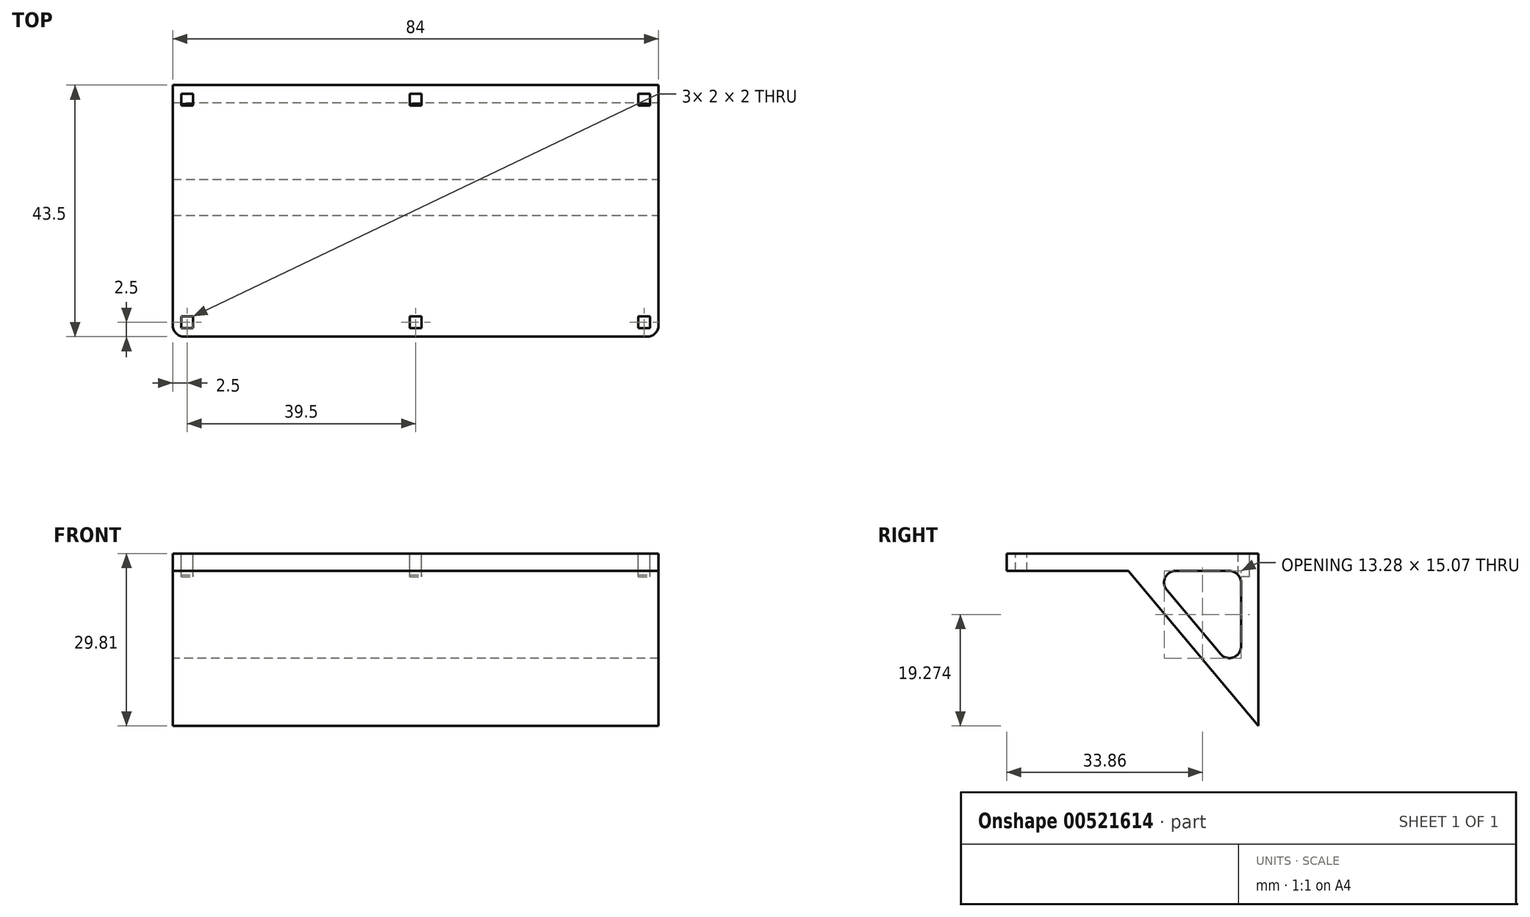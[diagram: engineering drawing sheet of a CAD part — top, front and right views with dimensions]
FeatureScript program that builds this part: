
annotation { "Feature Type Name" : "Feature", "Feature Type Description" : "" }
export const myFeature = defineFeature(function(context is Context, id is Id, definition is map)
    precondition{}
    {
        {
            var Q0;
            Q0=qCreatedBy(makeId("Right.planeOp"),FACE);
            var sketch = newSketch(context, id + "F0", { "sketchPlane" : qUnion([Q0])});
            skLineSegment(sketch, "E0", {"start": v(0, 0) * mm, "end": v(21, 0) * mm});
            skLineSegment(sketch, "E1", {"start": v(21, 0) * mm, "end": v(43.5, -26.81) * mm});
            skLineSegment(sketch, "E2.0", {"start": v(0, 3) * mm, "end": v(21, 3) * mm});
            skLineSegment(sketch, "E3.0", {"start": v(24.92, 0) * mm, "end": v(40.5, -18.57) * mm});
            skLineSegment(sketch, "E4", {"start": v(0, 3) * mm, "end": v(0, 0) * mm});
            skLineSegment(sketch, "E5", {"start": v(21, 3) * mm, "end": v(43.5, 3) * mm});
            skLineSegment(sketch, "E6", {"start": v(43.5, -26.81) * mm, "end": v(43.5, 3) * mm});
            skLineSegment(sketch, "E7", {"start": v(24.92, 0) * mm, "end": v(40.5, 0) * mm});
            skLineSegment(sketch, "E8.trimOffspring", {"start": v(40.5, -18.57) * mm, "end": v(40.5, 0) * mm});
            skSolve(sketch);
        }
        {
            var Q0;
            Q0=makeQuery(id+"F0.imprint","IMPRINT",FACE,{"disambiguationData":[TD([[makeQuery(id+"F0.imprint","IMPRINT",EDGE,{"derivedFrom":sQuery(id+"F0.wireOp",EDGE,"HT0NIHEq-mOGw-AMZ3-bg6D-jiP4Rz8PsHoc.bottom")}),1.0]])]});
            var Q1;
            Q1=makeQuery(id+"F0.imprint","IMPRINT",FACE,{"disambiguationData":[TD([[makeQuery(id+"F0.imprint","IMPRINT",EDGE,{"derivedFrom":sQuery(id+"F0.wireOp",EDGE,"E0")}),1.0]])]});
            var Q2;
            Q2=makeQuery(id+"F0.imprint","IMPRINT",FACE,{"disambiguationData":[TD([[makeQuery(id+"F0.imprint","IMPRINT",EDGE,{"derivedFrom":sQuery(id+"F0.wireOp",EDGE,"E2.0")}),1.0]])]});
            var Q3;
            {var subQ3=sQuery(id+"F0.wireOp",EDGE,"2d6a4896-3aa3-4e97-b98b-c350a894f704.0");Q3=makeQuery(id+"F0.imprint","IMPRINT",FACE,{"disambiguationData":[TD([[makeQuery(id+"F0.imprint","IMPRINT",EDGE,{"derivedFrom":subQ3}),1.0]])]});}
            extrude(context, id + "F1", {"entities" : qUnion([Q0, Q1, Q2, Q3]), "oppositeDirection" : true, "depth" : 84 * mm, "offsetDistance" : 25 * mm});
        }
        {
            var Q0;
            Q0=makeQuery(id+"F1.opExtrude","CAP_EDGE",EDGE,{"disambiguationData":[OSD([sQuery(id+"F0.wireOp",EDGE,"E4"),sQuery(id+"F0.wireOp",EDGE,"HT0NIHEq-mOGw-AMZ3-bg6D-jiP4Rz8PsHoc.left"),sQuery(id+"F0.wireOp",EDGE,"zdLE2qqB-wnvT-7mFk-4lY0-9LTzI25NRc8D")])],"isStart":true});
            var Q1;
            Q1=makeQuery(id+"F1.opExtrude","CAP_EDGE",EDGE,{"disambiguationData":[OSD([sQuery(id+"F0.wireOp",EDGE,"E4"),sQuery(id+"F0.wireOp",EDGE,"HT0NIHEq-mOGw-AMZ3-bg6D-jiP4Rz8PsHoc.left"),sQuery(id+"F0.wireOp",EDGE,"zdLE2qqB-wnvT-7mFk-4lY0-9LTzI25NRc8D")])],"isStart":false});
            var Q2;
            Q2=makeQuery(id+"F1.opExtrude","CAP_EDGE",EDGE,{"disambiguationData":[OSD([sQuery(id+"F0.wireOp",EDGE,"HT0NIHEq-mOGw-AMZ3-bg6D-jiP4Rz8PsHoc.right"),sQuery(id+"F0.wireOp",EDGE,"6K6W7r0D-Gj0a-smYx-N5Y3-3RsnSGkDnLhq")])],"isStart":true});
            var Q3;
            Q3=makeQuery(id+"F1.opExtrude","CAP_EDGE",EDGE,{"disambiguationData":[OSD([sQuery(id+"F0.wireOp",EDGE,"HT0NIHEq-mOGw-AMZ3-bg6D-jiP4Rz8PsHoc.right"),sQuery(id+"F0.wireOp",EDGE,"6K6W7r0D-Gj0a-smYx-N5Y3-3RsnSGkDnLhq")])],"isStart":false});
            fillet(context, id + "F2", {"entities" : qUnion([Q0, Q1, Q2, Q3]), "radius" : 2 * mm, "tangentPropagation" : true, "allowEdgeOverflow" : false});
        }
        {
            var Q0;
            Q0=makeQuery(id+"F1.opExtrude","SWEPT_EDGE",EDGE,{"disambiguationData":[OSD([sQuery(id+"F0.wireOp",EDGE,"E3.0"),sQuery(id+"F0.wireOp",EDGE,"ABOKRz2A-O9Wl-NYz3-LtdV-byAFksUtFqJd")])]});
            var Q1;
            Q1=makeQuery(id+"F1.opExtrude","SWEPT_EDGE",EDGE,{"disambiguationData":[OSD([sQuery(id+"F0.wireOp",EDGE,"E7"),sQuery(id+"F0.wireOp",EDGE,"E8.trimOffspring")])]});
            fillet(context, id + "F3", {"entities" : qUnion([Q0, Q1]), "radius" : 2 * mm, "tangentPropagation" : true, "allowEdgeOverflow" : false});
        }
        {
            var Q0;
            Q0=makeQuery(id+"F1.opExtrude","SWEPT_FACE",FACE,{"disambiguationData":[OSD([sQuery(id+"F0.wireOp",EDGE,"E2.0"),sQuery(id+"F0.wireOp",EDGE,"E5")])]});
            var sketch = newSketch(context, id + "F4", { "sketchPlane" : qUnion([Q0])});
            skLineSegment(sketch, "E9.0.0", {"start": v(-44.5, 43.5) * mm, "end": v(-44.5, 38.5) * mm, "construction": true});
            skLineSegment(sketch, "E9.0.1", {"start": v(-44.5, 38.5) * mm, "end": v(-39.5, 38.5) * mm, "construction": true});
            skLineSegment(sketch, "E9.0.2", {"start": v(-39.5, 38.5) * mm, "end": v(-39.5, 43.5) * mm, "construction": true});
            skLineSegment(sketch, "E9.0.3", {"start": v(-39.5, 43.5) * mm, "end": v(-44.5, 43.5) * mm, "construction": true});
            skLineSegment(sketch, "E10.0.0", {"start": v(0, 38.5) * mm, "end": v(0, 41.5) * mm, "construction": true});
            skArc(sketch, "E10.0.1", {"start": v(0, 41.5) * mm, "mid": v(-0.59, 42.91) * mm, "end": v(-2, 43.5) * mm, "construction": true});
            skLineSegment(sketch, "E10.0.2", {"start": v(-2, 43.5) * mm, "end": v(-5, 43.5) * mm, "construction": true});
            skLineSegment(sketch, "E10.0.3", {"start": v(-5, 43.5) * mm, "end": v(-5, 38.5) * mm, "construction": true});
            skLineSegment(sketch, "E10.0.4", {"start": v(-5, 38.5) * mm, "end": v(0, 38.5) * mm, "construction": true});
            skLineSegment(sketch, "E11.0.0", {"start": v(-5, 0) * mm, "end": v(-2, 0) * mm, "construction": true});
            skArc(sketch, "E11.0.1", {"start": v(-2, 0) * mm, "mid": v(-0.59, 0.59) * mm, "end": v(0, 2) * mm, "construction": true});
            skLineSegment(sketch, "E11.0.2", {"start": v(0, 2) * mm, "end": v(0, 5) * mm, "construction": true});
            skLineSegment(sketch, "E11.0.3", {"start": v(0, 5) * mm, "end": v(-5, 5) * mm, "construction": true});
            skLineSegment(sketch, "E11.0.4", {"start": v(-5, 5) * mm, "end": v(-5, 0) * mm, "construction": true});
            skLineSegment(sketch, "E12.0.0", {"start": v(-44.5, 43.5) * mm, "end": v(-44.5, -38.5) * mm, "construction": true});
            skLineSegment(sketch, "E12.0.1", {"start": v(-44.5, -38.5) * mm, "end": v(-39.5, -38.5) * mm, "construction": true});
            skLineSegment(sketch, "E12.0.2", {"start": v(-39.5, -38.5) * mm, "end": v(-39.5, 43.5) * mm, "construction": true});
            skLineSegment(sketch, "E13.0.0", {"start": v(-84, 5) * mm, "end": v(-84, 2) * mm, "construction": true});
            skArc(sketch, "E13.0.1", {"start": v(-84, 2) * mm, "mid": v(-83.41, 0.59) * mm, "end": v(-82, 0) * mm, "construction": true});
            skLineSegment(sketch, "E13.0.2", {"start": v(-82, 0) * mm, "end": v(-79, 0) * mm, "construction": true});
            skLineSegment(sketch, "E13.0.3", {"start": v(-79, 0) * mm, "end": v(-79, 5) * mm, "construction": true});
            skLineSegment(sketch, "E13.0.4", {"start": v(-79, 5) * mm, "end": v(-84, 5) * mm, "construction": true});
            skLineSegment(sketch, "E14.0.0", {"start": v(-79, 43.5) * mm, "end": v(-82, 43.5) * mm, "construction": true});
            skArc(sketch, "E14.0.1", {"start": v(-82, 43.5) * mm, "mid": v(-83.41, 42.91) * mm, "end": v(-84, 41.5) * mm, "construction": true});
            skLineSegment(sketch, "E14.0.2", {"start": v(-84, 41.5) * mm, "end": v(-84, 38.5) * mm, "construction": true});
            skLineSegment(sketch, "E14.0.3", {"start": v(-84, 38.5) * mm, "end": v(-79, 38.5) * mm, "construction": true});
            skLineSegment(sketch, "E14.0.4", {"start": v(-79, 38.5) * mm, "end": v(-79, 43.5) * mm, "construction": true});
            skLineSegment(sketch, "E15.bottom", {"start": v(-41, 42) * mm, "end": v(-43, 42) * mm});
            skLineSegment(sketch, "E15.top", {"start": v(-41, 40) * mm, "end": v(-43, 40) * mm});
            skLineSegment(sketch, "E15.left", {"start": v(-41, 42) * mm, "end": v(-41, 40) * mm});
            skLineSegment(sketch, "E15.right", {"start": v(-43, 42) * mm, "end": v(-43, 40) * mm});
            skPoint(sketch, "E15.middle", {"position": v(-42, 41) * mm});
            skPoint(sketch, "E15.middle.positionSnap0", {"position": v(-42, 43.5) * mm});
            skPoint(sketch, "E15.middle.positionSnap1", {"position": v(-44.5, 41) * mm});
            skPoint(sketch, "E15.centerSnap0", {"position": v(-42, 43.39) * mm});
            skPoint(sketch, "E15.centerSnap1", {"position": v(-44.5, 41) * mm});
            skLineSegment(sketch, "E16.bottom", {"start": v(-1.5, 40) * mm, "end": v(-3.5, 40) * mm});
            skLineSegment(sketch, "E16.top", {"start": v(-1.5, 42) * mm, "end": v(-3.5, 42) * mm});
            skLineSegment(sketch, "E16.left", {"start": v(-1.5, 40) * mm, "end": v(-1.5, 42) * mm});
            skLineSegment(sketch, "E16.right", {"start": v(-3.5, 40) * mm, "end": v(-3.5, 42) * mm});
            skPoint(sketch, "E16.middle", {"position": v(-2.5, 41) * mm});
            skPoint(sketch, "E16.middle.positionSnap0", {"position": v(-2.5, 38.5) * mm});
            skPoint(sketch, "E16.middle.positionSnap1", {"position": v(-5, 41) * mm});
            skPoint(sketch, "E16.centerSnap0", {"position": v(-2.5, 38.5) * mm});
            skPoint(sketch, "E16.centerSnap1", {"position": v(-5, 41) * mm});
            skLineSegment(sketch, "E17.bottom", {"start": v(-1.5, 3.5) * mm, "end": v(-3.5, 3.5) * mm});
            skLineSegment(sketch, "E17.top", {"start": v(-1.5, 1.5) * mm, "end": v(-3.5, 1.5) * mm});
            skLineSegment(sketch, "E17.left", {"start": v(-1.5, 3.5) * mm, "end": v(-1.5, 1.5) * mm});
            skLineSegment(sketch, "E17.right", {"start": v(-3.5, 3.5) * mm, "end": v(-3.5, 1.5) * mm});
            skPoint(sketch, "E17.middle", {"position": v(-2.5, 2.5) * mm});
            skPoint(sketch, "E17.middle.positionSnap0", {"position": v(-2.5, 5) * mm});
            skPoint(sketch, "E17.middle.positionSnap1", {"position": v(-5, 2.5) * mm});
            skPoint(sketch, "E17.centerSnap0", {"position": v(-2.5, 5) * mm});
            skPoint(sketch, "E17.centerSnap1", {"position": v(-5, 2.5) * mm});
            skLineSegment(sketch, "E18.bottom", {"start": v(-41, 3.5) * mm, "end": v(-43, 3.5) * mm});
            skLineSegment(sketch, "E18.top", {"start": v(-41, 1.5) * mm, "end": v(-43, 1.5) * mm});
            skLineSegment(sketch, "E18.left", {"start": v(-41, 3.5) * mm, "end": v(-41, 1.5) * mm});
            skLineSegment(sketch, "E18.right", {"start": v(-43, 3.5) * mm, "end": v(-43, 1.5) * mm});
            skPoint(sketch, "E18.middle", {"position": v(-42, 2.5) * mm});
            skPoint(sketch, "E18.middle.positionSnap0", {"position": v(-44.5, 2.5) * mm});
            skPoint(sketch, "E18.centerSnap0", {"position": v(-44.5, 2.5) * mm});
            skLineSegment(sketch, "E19.bottom", {"start": v(-80.5, 3.5) * mm, "end": v(-82.5, 3.5) * mm});
            skLineSegment(sketch, "E19.top", {"start": v(-80.5, 1.5) * mm, "end": v(-82.5, 1.5) * mm});
            skLineSegment(sketch, "E19.left", {"start": v(-80.5, 3.5) * mm, "end": v(-80.5, 1.5) * mm});
            skLineSegment(sketch, "E19.right", {"start": v(-82.5, 3.5) * mm, "end": v(-82.5, 1.5) * mm});
            skPoint(sketch, "E19.middle", {"position": v(-81.5, 2.5) * mm});
            skPoint(sketch, "E19.middle.positionSnap0", {"position": v(-79, 2.5) * mm});
            skPoint(sketch, "E19.middle.positionSnap1", {"position": v(-81.5, 5) * mm});
            skPoint(sketch, "E19.centerSnap0", {"position": v(-79, 2.5) * mm});
            skPoint(sketch, "E19.centerSnap1", {"position": v(-81.5, 5) * mm});
            skLineSegment(sketch, "E20.bottom", {"start": v(-80.5, 42) * mm, "end": v(-82.5, 42) * mm});
            skLineSegment(sketch, "E20.top", {"start": v(-80.5, 40) * mm, "end": v(-82.5, 40) * mm});
            skLineSegment(sketch, "E20.left", {"start": v(-80.5, 42) * mm, "end": v(-80.5, 40) * mm});
            skLineSegment(sketch, "E20.right", {"start": v(-82.5, 42) * mm, "end": v(-82.5, 40) * mm});
            skPoint(sketch, "E20.middle", {"position": v(-81.5, 41) * mm});
            skPoint(sketch, "E20.middle.positionSnap0", {"position": v(-79, 41) * mm});
            skPoint(sketch, "E20.middle.positionSnap1", {"position": v(-81.5, 38.5) * mm});
            skPoint(sketch, "E20.centerSnap0", {"position": v(-79, 41) * mm});
            skPoint(sketch, "E20.centerSnap1", {"position": v(-81.5, 38.5) * mm});
            skLineSegment(sketch, "E21.0", {"start": v(-84, 43.5) * mm, "end": v(0, 43.5) * mm, "construction": true});
            skSolve(sketch);
        }
        {
            var Q0;
            Q0 = qSketchRegion(id + "F4", true);
            extrude(context, id + "F5", {"entities" : qUnion([Q0]), "operationType" : NewBodyOperationType.REMOVE, "oppositeDirection" : true, "depth" : 4 * mm, "offsetDistance" : 25 * mm});
        }
    });
